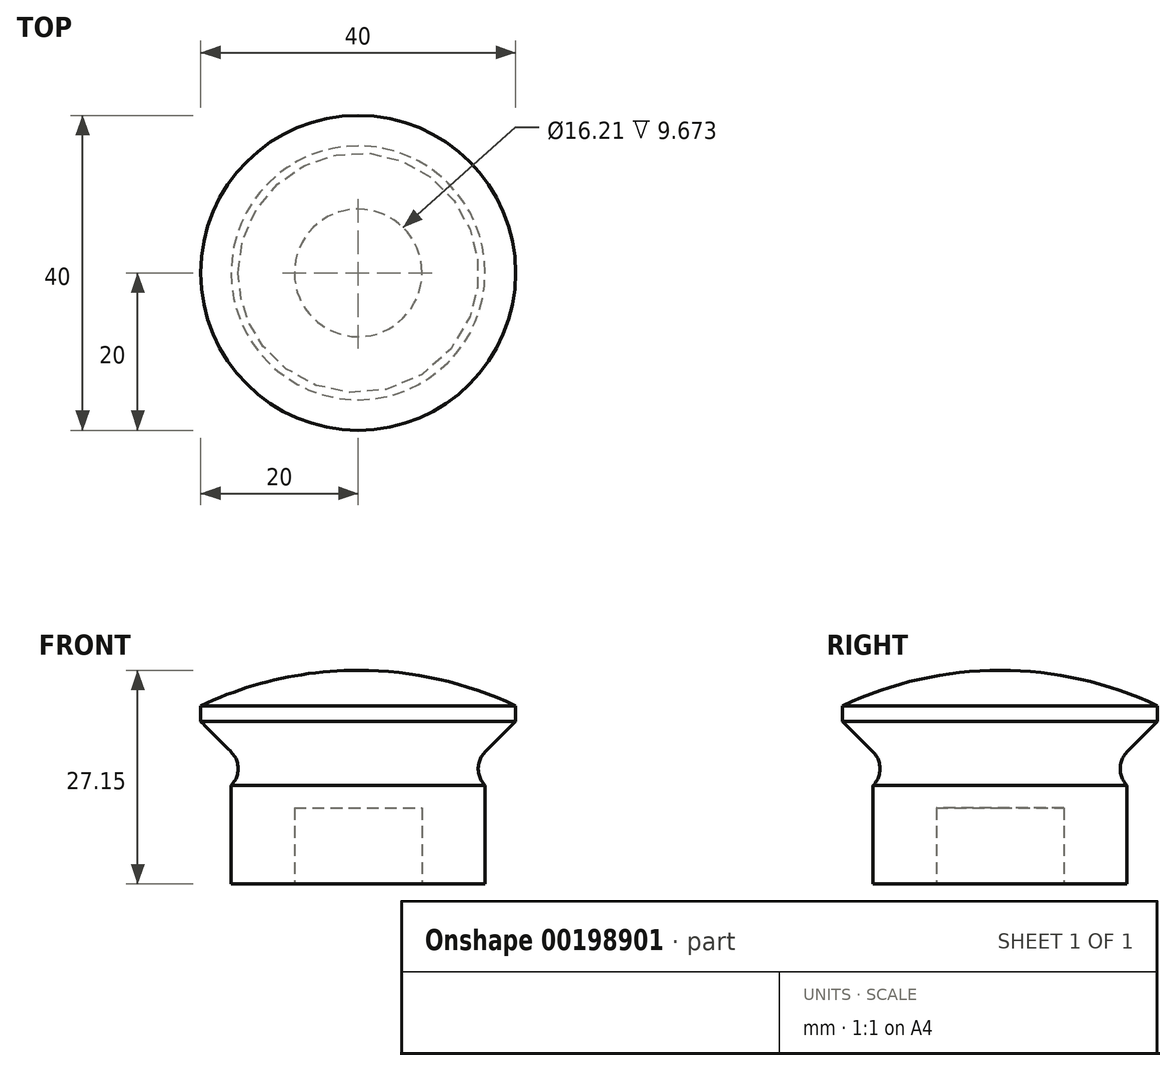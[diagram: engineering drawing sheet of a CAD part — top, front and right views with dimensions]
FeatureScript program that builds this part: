
annotation { "Feature Type Name" : "Feature", "Feature Type Description" : "" }
export const myFeature = defineFeature(function(context is Context, id is Id, definition is map)
    precondition{}
    {
        {
            var Q0;
            Q0=qCreatedBy(makeId("Front.planeOp"),FACE);
            var sketch = newSketch(context, id + "F0", { "sketchPlane" : qUnion([Q0])});
            skLineSegment(sketch, "E0", {"start": v(0, 9.67) * mm, "end": v(-8.1, 9.67) * mm});
            skLineSegment(sketch, "E1", {"start": v(-8.1, 9.67) * mm, "end": v(-8.1, 0) * mm});
            skLineSegment(sketch, "E2", {"start": v(-8.1, 0) * mm, "end": v(-16.13, 0) * mm});
            skLineSegment(sketch, "E3", {"start": v(-16.13, 0) * mm, "end": v(-16.13, 12.54) * mm});
            skArc(sketch, "E4", {"start": v(-16.13, 12.54) * mm, "mid": v(-15.25, 14.66) * mm, "end": v(-16.13, 16.78) * mm});
            skLineSegment(sketch, "E5", {"start": v(-16.13, 16.78) * mm, "end": v(-20, 20.65) * mm});
            skLineSegment(sketch, "E6", {"start": v(-20, 20.65) * mm, "end": v(-20, 22.65) * mm});
            skArc(sketch, "E7", {"start": v(0, 27.15) * mm, "mid": v(-10.25, 26.01) * mm, "end": v(-20, 22.65) * mm});
            skLineSegment(sketch, "E8", {"start": v(0, 0) * mm, "end": v(0, 33.04) * mm, "construction": true});
            skPoint(sketch, "E9.orphan", {"position": v(20, 22.65) * mm});
            skLineSegment(sketch, "E10", {"start": v(0, 27.15) * mm, "end": v(0, 9.67) * mm});
            skSolve(sketch);
        }
        {
            var Q0;
            Q0 = qSketchRegion(id + "F0", true);
            var Q1;
            Q1=sQuery(id+"F0.wireOp",EDGE,"E8");
            revolve(context, id + "F1", {"entities" : qUnion([Q0]), "axis" : qUnion([Q1]), "revolveType" : RevolveType.FULL});
        }
    });
